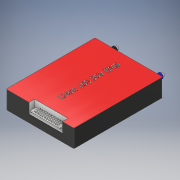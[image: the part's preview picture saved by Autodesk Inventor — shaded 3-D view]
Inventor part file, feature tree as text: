
AUTODESK INVENTOR PART (.ipt)
format: ipt  version: 2019.4 (Build 234330000, 330)  size: 615,424 bytes
history: native  units: mm
features: extrude x5, sketch x4, emboss x1, fillet x1
ambient origin geometry x8: Origin, YZ Plane, XZ Plane, XY Plane, X Axis, Y Axis, Z Axis, Center Point
bodies: Solid1 (feature_tree)
feature tree (11):
  extrude  "Extrusion1"  Depth=80.0mm
  sketch  "Sketch2"  dims[d2=16.0mm d3=0.0mm d4=30.0mm]
  extrude  "Extrusion2"  Depth=16.0mm
  extrude  "Extrusion3"  Depth=1.0mm TaperAngle=0.0deg
  emboss  "Emboss1"
  fillet  "Fillet1"  Radius=1.0mm
  sketch  "Sketch4"  dims[d13=1.0mm d14=0.5mm d15=2.0mm d16=1.0mm d17=2.5mm d18=5.0mm d19=0.0mm d20=3.0mm d21=3.0mm d22=0.1mm d23=0.0mm d24=1.0mm d26=5.0mm d28=10.0mm d29=8.0mm d30=8.0mm d31=0.0mm d32=3.06mm d33=10.0mm d34=0.0mm]
  extrude  "Extrusion4"  Depth=10.0mm
  extrude  "Extrusion5"  Depth=2.0mm
  sketch  "Sketch1"  dims[d0=61.0mm d1=80.0mm]
  sketch  "Sketch3"  dims[d5=5.0mm d6=9.0mm d7=0.0mm d12=1.0mm]
